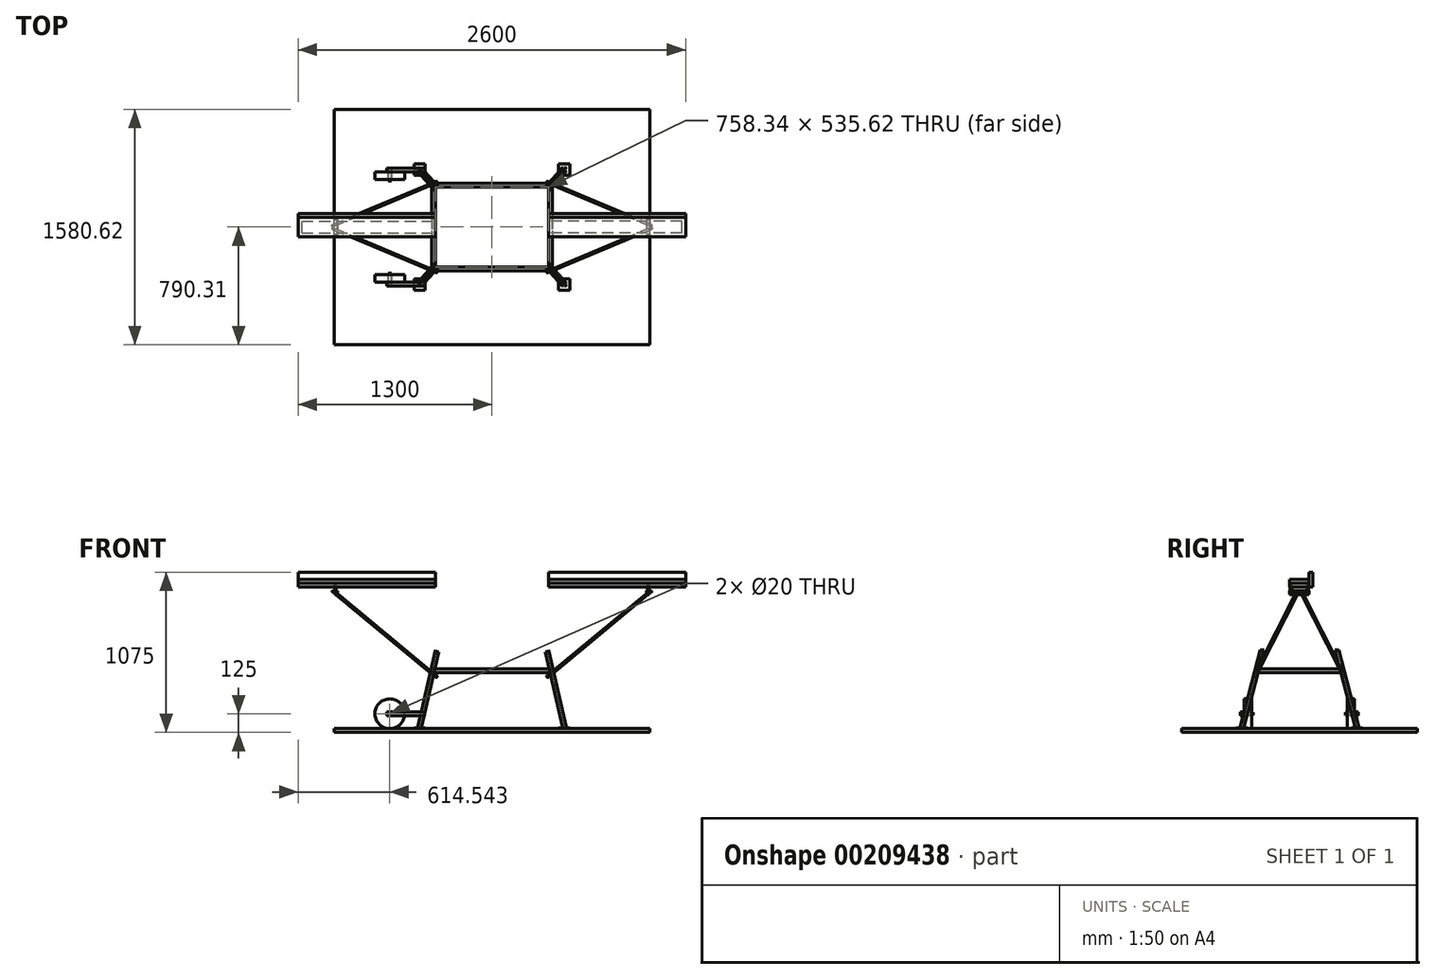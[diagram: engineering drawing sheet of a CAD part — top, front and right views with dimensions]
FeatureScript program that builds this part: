
annotation { "Feature Type Name" : "Feature", "Feature Type Description" : "" }
export const myFeature = defineFeature(function(context is Context, id is Id, definition is map)
    precondition{}
    {
        {
            var Q0;
            Q0=qCreatedBy(makeId("Top.planeOp"),FACE);
            var sketch = newSketch(context, id + "F0", { "sketchPlane" : qUnion([Q0])});
            skLineSegment(sketch, "E0.bottom", {"start": v(300, -175) * mm, "end": v(-300, -175) * mm});
            skLineSegment(sketch, "E0.top", {"start": v(300, 175) * mm, "end": v(-300, 175) * mm});
            skLineSegment(sketch, "E0.left", {"start": v(300, -175) * mm, "end": v(300, 175) * mm});
            skLineSegment(sketch, "E0.right", {"start": v(-300, -175) * mm, "end": v(-300, 175) * mm});
            skPoint(sketch, "E0.middle", {"position": v(0, 0) * mm});
            skSolve(sketch);
        }
        {
            var Q0;
            Q0 = qSketchRegion(id + "F0", true);
            extrude(context, id + "F1", {"entities" : qUnion([Q0]), "depth" : 100 * mm});
        }
        {
            var Q0;
            Q0=qCreatedBy(makeId("Top.planeOp"),FACE);
            cPlane(context, id + "F2", {"entities" : qUnion([Q0]), "cplaneType" : CPlaneType.OFFSET, "offset" : 900 * mm, "oppositeDirection" : true, "width" : 150 * mm, "height" : 150 * mm});
        }
        {
            var Q0;
            Q0=qCreatedBy(id+"F2.planeOp",FACE);
            var sketch = newSketch(context, id + "F3", { "sketchPlane" : qUnion([Q0])});
            skLineSegment(sketch, "E1.bottom", {"start": v(1059.42, -790.3) * mm, "end": v(-1059.42, -790.3) * mm});
            skLineSegment(sketch, "E1.top", {"start": v(1059.42, 790.3) * mm, "end": v(-1059.42, 790.3) * mm});
            skLineSegment(sketch, "E1.left", {"start": v(1059.42, -790.3) * mm, "end": v(1059.42, 790.3) * mm});
            skLineSegment(sketch, "E1.right", {"start": v(-1059.42, -790.3) * mm, "end": v(-1059.42, 790.3) * mm});
            skPoint(sketch, "E1.middle", {"position": v(0, 0) * mm});
            skSolve(sketch);
        }
        {
            var Q0;
            Q0 = qSketchRegion(id + "F3", true);
            extrude(context, id + "F4", {"entities" : qUnion([Q0]), "oppositeDirection" : true, "depth" : 25 * mm});
        }
        {
            var Q0;
            Q0=makeQuery(id+"F1.opExtrude","CAP_FACE",FACE,{"disambiguationData":[OSD([sQuery(id+"F0.wireOp",EDGE,"E0.bottom"),sQuery(id+"F0.wireOp",EDGE,"E0.top"),sQuery(id+"F0.wireOp",EDGE,"E0.left"),sQuery(id+"F0.wireOp",EDGE,"E0.right")])],"isStart":true});
            var sketch = newSketch(context, id + "F5", { "sketchPlane" : qUnion([Q0])});
            skLineSegment(sketch, "E2.bottom", {"start": v(-300, 175) * mm, "end": v(300, 175) * mm});
            skLineSegment(sketch, "E2.top", {"start": v(-300, -175) * mm, "end": v(300, -175) * mm});
            skLineSegment(sketch, "E2.left", {"start": v(-300, 175) * mm, "end": v(-300, -175) * mm});
            skLineSegment(sketch, "E2.right", {"start": v(300, 175) * mm, "end": v(300, -175) * mm});
            skLineSegment(sketch, "E3.0", {"start": v(-275, 150) * mm, "end": v(275, 150) * mm});
            skLineSegment(sketch, "E3.1", {"start": v(-275, 150) * mm, "end": v(-275, -150) * mm});
            skLineSegment(sketch, "E3.2", {"start": v(-275, -150) * mm, "end": v(275, -150) * mm});
            skLineSegment(sketch, "E3.3", {"start": v(275, 150) * mm, "end": v(275, -150) * mm});
            skSolve(sketch);
        }
        {
            var Q0;
            Q0 = qSketchRegion(id + "F5", true);
            extrude(context, id + "F6", {"entities" : qUnion([Q0]), "depth" : 25 * mm});
        }
        {
            var Q0;
            Q0=makeQuery(id+"F6.opExtrude","CAP_FACE",FACE,{"disambiguationData":[OSD([sQuery(id+"F5.wireOp",EDGE,"E2.bottom"),sQuery(id+"F5.wireOp",EDGE,"E2.top"),sQuery(id+"F5.wireOp",EDGE,"E2.left"),sQuery(id+"F5.wireOp",EDGE,"E2.right"),sQuery(id+"F5.wireOp",EDGE,"E3.0"),sQuery(id+"F5.wireOp",EDGE,"E3.1"),sQuery(id+"F5.wireOp",EDGE,"E3.2"),sQuery(id+"F5.wireOp",EDGE,"E3.3")])],"isStart":false});
            var sketch = newSketch(context, id + "F7", { "sketchPlane" : qUnion([Q0])});
            skLineSegment(sketch, "E4.bottom", {"start": v(-297, 172) * mm, "end": v(297, 172) * mm});
            skLineSegment(sketch, "E4.top", {"start": v(-297, -172) * mm, "end": v(297, -172) * mm});
            skLineSegment(sketch, "E4.left", {"start": v(-297, 172) * mm, "end": v(-297, -172) * mm});
            skLineSegment(sketch, "E4.right", {"start": v(297, 172) * mm, "end": v(297, -172) * mm});
            skSolve(sketch);
        }
        {
            var Q0;
            Q0 = qSketchRegion(id + "F7", true);
            extrude(context, id + "F8", {"entities" : qUnion([Q0]), "operationType" : NewBodyOperationType.REMOVE, "oppositeDirection" : true, "depth" : 22 * mm});
        }
        {
            var Q0;
            Q0=makeQuery(id+"F4.opExtrude","CAP_FACE",FACE,{"disambiguationData":[OSD([sQuery(id+"F3.wireOp",EDGE,"E1.bottom"),sQuery(id+"F3.wireOp",EDGE,"E1.top"),sQuery(id+"F3.wireOp",EDGE,"E1.left"),sQuery(id+"F3.wireOp",EDGE,"E1.right")])],"isStart":true});
            var sketch = newSketch(context, id + "F9", { "sketchPlane" : qUnion([Q0])});
            skLineSegment(sketch, "E5.bottom", {"start": v(500, -400) * mm, "end": v(-500, -400) * mm, "construction": true});
            skLineSegment(sketch, "E5.top", {"start": v(500, 400) * mm, "end": v(-500, 400) * mm, "construction": true});
            skLineSegment(sketch, "E5.left", {"start": v(500, -400) * mm, "end": v(500, 400) * mm, "construction": true});
            skLineSegment(sketch, "E5.right", {"start": v(-500, -400) * mm, "end": v(-500, 400) * mm, "construction": true});
            skPoint(sketch, "E5.middle", {"position": v(0, 0) * mm});
            skLineSegment(sketch, "E6", {"start": v(-500, -375) * mm, "end": v(-500, -400) * mm});
            skLineSegment(sketch, "E7", {"start": v(-500, -400) * mm, "end": v(-475, -400) * mm});
            skLineSegment(sketch, "E8", {"start": v(-475, -400) * mm, "end": v(-475, -397) * mm});
            skLineSegment(sketch, "E9", {"start": v(-475, -397) * mm, "end": v(-497, -397) * mm});
            skLineSegment(sketch, "E10", {"start": v(-497, -397) * mm, "end": v(-497, -375) * mm});
            skLineSegment(sketch, "E11", {"start": v(-497, -375) * mm, "end": v(-500, -375) * mm});
            skLineSegment(sketch, "E12", {"start": v(-868.34, 0) * mm, "end": v(770.25, 0) * mm, "construction": true});
            skLineSegment(sketch, "E13", {"start": v(0, 516.11) * mm, "end": v(0, -693.23) * mm, "construction": true});
            skPoint(sketch, "E13.startSnap0", {"position": v(0, 400) * mm});
            skSolve(sketch);
        }
        {
            var Q0;
            Q0=makeQuery(id+"F6.opExtrude","CAP_FACE",FACE,{"disambiguationData":[OSD([sQuery(id+"F5.wireOp",EDGE,"E2.bottom"),sQuery(id+"F5.wireOp",EDGE,"E2.top"),sQuery(id+"F5.wireOp",EDGE,"E2.left"),sQuery(id+"F5.wireOp",EDGE,"E2.right"),sQuery(id+"F5.wireOp",EDGE,"E3.0"),sQuery(id+"F5.wireOp",EDGE,"E3.1"),sQuery(id+"F5.wireOp",EDGE,"E3.2"),sQuery(id+"F5.wireOp",EDGE,"E3.3")])],"isStart":false});
            var sketch = newSketch(context, id + "F10", { "sketchPlane" : qUnion([Q0])});
            skLineSegment(sketch, "E14", {"start": v(-300, 175) * mm, "end": v(-300, 150) * mm});
            skLineSegment(sketch, "E15", {"start": v(-300, 150) * mm, "end": v(-297, 150) * mm});
            skLineSegment(sketch, "E16", {"start": v(-297, 150) * mm, "end": v(-297, 172) * mm});
            skLineSegment(sketch, "E17", {"start": v(-297, 172) * mm, "end": v(-275, 172) * mm});
            skLineSegment(sketch, "E18", {"start": v(-275, 172) * mm, "end": v(-275, 175) * mm});
            skLineSegment(sketch, "E19", {"start": v(-275, 175) * mm, "end": v(-300, 175) * mm});
            skSolve(sketch);
        }
        {
            var Q1;
            Q1 = qSketchRegion(id + "F9", true);
            var Q2;
            Q2 = qSketchRegion(id + "F10", true);
            loft(context, id + "F11", {"sheetProfilesArray" : [{ "sheetProfileEntities" : qUnion([Q1]) }, { "sheetProfileEntities" : qUnion([Q2]) }]});
        }
        {
            var Q0;
            Q0=makeQuery(id+"F11.opLoft","SWEPT_BODY",BODY,{"disambiguationData":[OSD([makeQuery(id+"F9.imprint","IMPRINT",FACE,{"disambiguationData":[TD([[makeQuery(id+"F9.imprint","IMPRINT",EDGE,{"derivedFrom":sQuery(id+"F9.wireOp",EDGE,"E6")}),1.0]])]}),makeQuery(id+"F10.imprint","IMPRINT",FACE,{"disambiguationData":[TD([[makeQuery(id+"F10.imprint","IMPRINT",EDGE,{"derivedFrom":sQuery(id+"F10.wireOp",EDGE,"E14")}),1.0]])]})])]});
            var Q1;
            Q1=qCreatedBy(makeId("Right.planeOp"),FACE);
            mirror(context, id + "F12", {"entities" : qUnion([Q0]), "mirrorPlane" : qUnion([Q1])});
        }
        {
            var Q0;
            Q0=makeQuery(id+"F11.opLoft","SWEPT_BODY",BODY,{"disambiguationData":[OSD([makeQuery(id+"F9.imprint","IMPRINT",FACE,{"disambiguationData":[TD([[makeQuery(id+"F9.imprint","IMPRINT",EDGE,{"derivedFrom":sQuery(id+"F9.wireOp",EDGE,"E6")}),1.0]])]}),makeQuery(id+"F10.imprint","IMPRINT",FACE,{"disambiguationData":[TD([[makeQuery(id+"F10.imprint","IMPRINT",EDGE,{"derivedFrom":sQuery(id+"F10.wireOp",EDGE,"E14")}),1.0]])]})])]});
            var Q1;
            Q1=makeQuery(id+"F12.opPattern","COPY",BODY,{"derivedFrom":makeQuery(id+"F11.opLoft","SWEPT_BODY",BODY,{"disambiguationData":[OSD([makeQuery(id+"F9.imprint","IMPRINT",FACE,{"disambiguationData":[TD([[makeQuery(id+"F9.imprint","IMPRINT",EDGE,{"derivedFrom":sQuery(id+"F9.wireOp",EDGE,"E6")}),1.0]])]}),makeQuery(id+"F10.imprint","IMPRINT",FACE,{"disambiguationData":[TD([[makeQuery(id+"F10.imprint","IMPRINT",EDGE,{"derivedFrom":sQuery(id+"F10.wireOp",EDGE,"E14")}),1.0]])]})])]}),"instanceName":"1"});
            var Q2;
            Q2=qCreatedBy(makeId("Front.planeOp"),FACE);
            mirror(context, id + "F13", {"entities" : qUnion([Q0, Q1]), "mirrorPlane" : qUnion([Q2])});
        }
        {
            assignVariable(context, id + "F14", {"name" : "MidLevel", "anyValue" : 500});
        }
        {
            var Q0;
            Q0=qCreatedBy(makeId("Top.planeOp"),FACE);
            cPlane(context, id + "F15", {"entities" : qUnion([Q0]), "cplaneType" : CPlaneType.OFFSET, "offset" : (getVariable(context, 'MidLevel')) * mm, "oppositeDirection" : true, "width" : 150 * mm, "height" : 150 * mm});
        }
        {
            var Q0;
            Q0=qCreatedBy(id+"F15.planeOp",FACE);
            var sketch = newSketch(context, id + "F16", { "sketchPlane" : qUnion([Q0])});
            skLineSegment(sketch, "E20.bottom", {"start": v(404.17, 292.8) * mm, "end": v(-404.17, 292.8) * mm});
            skLineSegment(sketch, "E20.top", {"start": v(404.17, -292.8) * mm, "end": v(-404.17, -292.8) * mm});
            skLineSegment(sketch, "E20.left", {"start": v(404.17, 292.8) * mm, "end": v(404.17, -292.8) * mm});
            skLineSegment(sketch, "E20.right", {"start": v(-404.17, 292.8) * mm, "end": v(-404.17, -292.8) * mm});
            skPoint(sketch, "E20.middle", {"position": v(0, 0) * mm});
            skSolve(sketch);
        }
        {
            var Q0;
            Q0 = qSketchRegion(id + "F16", true);
            extrude(context, id + "F17", {"entities" : qUnion([Q0]), "oppositeDirection" : true, "depth" : 25 * mm});
        }
        {
            var Q0;
            Q0=qCreatedBy(id+"F2.planeOp",FACE);
            var sketch = newSketch(context, id + "F18", { "sketchPlane" : qUnion([Q0])});
            skLineSegment(sketch, "E21.bottom", {"start": v(-522.96, -423.3) * mm, "end": v(-447.96, -423.3) * mm});
            skLineSegment(sketch, "E21.top", {"start": v(-522.96, -348.3) * mm, "end": v(-447.96, -348.3) * mm});
            skLineSegment(sketch, "E21.left", {"start": v(-522.96, -423.3) * mm, "end": v(-522.96, -348.3) * mm});
            skLineSegment(sketch, "E21.right", {"start": v(-447.96, -423.3) * mm, "end": v(-447.96, -348.3) * mm});
            skSolve(sketch);
        }
        {
            var Q0;
            Q0 = qSketchRegion(id + "F18", true);
            extrude(context, id + "F19", {"entities" : qUnion([Q0]), "depth" : 3 * mm});
        }
        {
            var Q0;
            Q0=makeQuery(id+"F19.opExtrude","SWEPT_BODY",BODY,{"disambiguationData":[OSD([sQuery(id+"F18.wireOp",EDGE,"E21.bottom"),sQuery(id+"F18.wireOp",EDGE,"E21.top"),sQuery(id+"F18.wireOp",EDGE,"E21.left"),sQuery(id+"F18.wireOp",EDGE,"E21.right")])]});
            var Q1;
            Q1=qCreatedBy(makeId("Front.planeOp"),FACE);
            mirror(context, id + "F20", {"entities" : qUnion([Q0]), "mirrorPlane" : qUnion([Q1])});
        }
        {
            var Q0;
            Q0=makeQuery(id+"F20.opPattern","COPY",BODY,{"derivedFrom":makeQuery(id+"F19.opExtrude","SWEPT_BODY",BODY,{"disambiguationData":[OSD([sQuery(id+"F18.wireOp",EDGE,"E21.bottom"),sQuery(id+"F18.wireOp",EDGE,"E21.top"),sQuery(id+"F18.wireOp",EDGE,"E21.left"),sQuery(id+"F18.wireOp",EDGE,"E21.right")])]}),"instanceName":"1"});
            var Q1;
            Q1=makeQuery(id+"F19.opExtrude","SWEPT_BODY",BODY,{"disambiguationData":[OSD([sQuery(id+"F18.wireOp",EDGE,"E21.bottom"),sQuery(id+"F18.wireOp",EDGE,"E21.top"),sQuery(id+"F18.wireOp",EDGE,"E21.left"),sQuery(id+"F18.wireOp",EDGE,"E21.right")])]});
            var Q2;
            Q2=qCreatedBy(makeId("Right.planeOp"),FACE);
            mirror(context, id + "F21", {"entities" : qUnion([Q0, Q1]), "mirrorPlane" : qUnion([Q2])});
        }
        {
            var Q0;
            Q0=makeQuery(id+"F1.opExtrude","CAP_FACE",FACE,{"disambiguationData":[OSD([sQuery(id+"F0.wireOp",EDGE,"E0.bottom"),sQuery(id+"F0.wireOp",EDGE,"E0.top"),sQuery(id+"F0.wireOp",EDGE,"E0.left"),sQuery(id+"F0.wireOp",EDGE,"E0.right")])],"isStart":false});
            var sketch = newSketch(context, id + "F22", { "sketchPlane" : qUnion([Q0])});
            skLineSegment(sketch, "E22.bottom", {"start": v(-1300, 65) * mm, "end": v(-300, 65) * mm});
            skLineSegment(sketch, "E22.top", {"start": v(-1300, -65) * mm, "end": v(-300, -65) * mm});
            skLineSegment(sketch, "E22.left", {"start": v(-1300, 65) * mm, "end": v(-1300, -65) * mm});
            skLineSegment(sketch, "E22.right", {"start": v(-300, 65) * mm, "end": v(-300, -65) * mm});
            skLineSegment(sketch, "E23", {"start": v(0, 0) * mm, "end": v(-555.69, 0) * mm, "construction": true});
            skSolve(sketch);
        }
        {
            var Q0;
            Q0 = qSketchRegion(id + "F22", true);
            extrude(context, id + "F23", {"entities" : qUnion([Q0]), "oppositeDirection" : true, "depth" : 25 * mm});
        }
        {
            var Q0;
            Q0=makeQuery(id+"F23.opExtrude","CAP_FACE",FACE,{"disambiguationData":[OSD([sQuery(id+"F22.wireOp",EDGE,"E22.bottom"),sQuery(id+"F22.wireOp",EDGE,"E22.top"),sQuery(id+"F22.wireOp",EDGE,"E22.left"),sQuery(id+"F22.wireOp",EDGE,"E22.right")])],"isStart":false});
            var sketch = newSketch(context, id + "F24", { "sketchPlane" : qUnion([Q0])});
            skLineSegment(sketch, "E24.bottom", {"start": v(-1300, 65) * mm, "end": v(-300, 65) * mm});
            skLineSegment(sketch, "E24.top", {"start": v(-1300, -65) * mm, "end": v(-300, -65) * mm});
            skLineSegment(sketch, "E24.left", {"start": v(-1300, 65) * mm, "end": v(-1300, -65) * mm});
            skLineSegment(sketch, "E24.right", {"start": v(-300, 65) * mm, "end": v(-300, -65) * mm});
            skLineSegment(sketch, "E25.0", {"start": v(-1275, 40) * mm, "end": v(-325, 40) * mm});
            skLineSegment(sketch, "E25.1", {"start": v(-1275, 40) * mm, "end": v(-1275, -40) * mm});
            skLineSegment(sketch, "E25.2", {"start": v(-1275, -40) * mm, "end": v(-325, -40) * mm});
            skLineSegment(sketch, "E25.3", {"start": v(-325, 40) * mm, "end": v(-325, -40) * mm});
            skSolve(sketch);
        }
        {
            var Q0;
            Q0 = qSketchRegion(id + "F24", true);
            extrude(context, id + "F25", {"entities" : qUnion([Q0]), "depth" : 25 * mm});
        }
        {
            var Q0;
            Q0=makeQuery(id+"F25.opExtrude","CAP_FACE",FACE,{"disambiguationData":[OSD([sQuery(id+"F24.wireOp",EDGE,"E24.bottom"),sQuery(id+"F24.wireOp",EDGE,"E24.top"),sQuery(id+"F24.wireOp",EDGE,"E24.left"),sQuery(id+"F24.wireOp",EDGE,"E24.right"),sQuery(id+"F24.wireOp",EDGE,"E25.0"),sQuery(id+"F24.wireOp",EDGE,"E25.1"),sQuery(id+"F24.wireOp",EDGE,"E25.2"),sQuery(id+"F24.wireOp",EDGE,"E25.3")])],"isStart":false});
            var sketch = newSketch(context, id + "F26", { "sketchPlane" : qUnion([Q0])});
            skLineSegment(sketch, "E26.bottom", {"start": v(-1297, 62) * mm, "end": v(-303, 62) * mm});
            skLineSegment(sketch, "E26.top", {"start": v(-1297, -62) * mm, "end": v(-303, -62) * mm});
            skLineSegment(sketch, "E26.left", {"start": v(-1297, 62) * mm, "end": v(-1297, -62) * mm});
            skLineSegment(sketch, "E26.right", {"start": v(-303, 62) * mm, "end": v(-303, -62) * mm});
            skSolve(sketch);
        }
        {
            var Q0;
            Q0 = qSketchRegion(id + "F26", true);
            extrude(context, id + "F27", {"entities" : qUnion([Q0]), "operationType" : NewBodyOperationType.REMOVE, "oppositeDirection" : true, "depth" : 22 * mm});
        }
        {
            var Q0;
            Q0=makeQuery(id+"F25.opExtrude","SWEPT_FACE",FACE,{"disambiguationData":[OSD([sQuery(id+"F24.wireOp",EDGE,"E24.top")])]});
            var sketch = newSketch(context, id + "F28", { "sketchPlane" : qUnion([Q0])});
            skLineSegment(sketch, "E27.bottom", {"start": v(300, 50) * mm, "end": v(1300, 50) * mm});
            skLineSegment(sketch, "E27.top", {"start": v(300, 150) * mm, "end": v(1300, 150) * mm});
            skLineSegment(sketch, "E27.left", {"start": v(300, 50) * mm, "end": v(300, 150) * mm});
            skLineSegment(sketch, "E27.right", {"start": v(1300, 50) * mm, "end": v(1300, 150) * mm});
            skSolve(sketch);
        }
        {
            var Q0;
            Q0 = qSketchRegion(id + "F28", true);
            extrude(context, id + "F29", {"entities" : qUnion([Q0]), "depth" : 25 * mm});
        }
        {
            var Q0;
            Q0=makeQuery(id+"F25.opExtrude","CAP_FACE",FACE,{"disambiguationData":[OSD([sQuery(id+"F24.wireOp",EDGE,"E24.bottom"),sQuery(id+"F24.wireOp",EDGE,"E24.top"),sQuery(id+"F24.wireOp",EDGE,"E24.left"),sQuery(id+"F24.wireOp",EDGE,"E24.right"),sQuery(id+"F24.wireOp",EDGE,"E25.0"),sQuery(id+"F24.wireOp",EDGE,"E25.1"),sQuery(id+"F24.wireOp",EDGE,"E25.2"),sQuery(id+"F24.wireOp",EDGE,"E25.3")])],"isStart":false});
            var sketch = newSketch(context, id + "F30", { "sketchPlane" : qUnion([Q0])});
            skCircle(sketch, "E28", {"center": v(-1050, 56) * mm, "radius": 6 * mm});
            skSolve(sketch);
        }
        {
            var Q0;
            Q0 = qSketchRegion(id + "F30", true);
            var Q1;
            Q1=makeQuery(id+"F23.opExtrude","CAP_FACE",FACE,{"disambiguationData":[OSD([sQuery(id+"F22.wireOp",EDGE,"E22.bottom"),sQuery(id+"F22.wireOp",EDGE,"E22.top"),sQuery(id+"F22.wireOp",EDGE,"E22.left"),sQuery(id+"F22.wireOp",EDGE,"E22.right")])],"isStart":false});
            extrude(context, id + "F31", {"entities" : qUnion([Q0]), "depth" : 50 * mm, "hasSecondDirection" : true, "secondDirectionBound" : SecondDirectionBoundingType.UP_TO_SURFACE, "secondDirectionOppositeDirection" : true, "secondDirectionBoundEntityFace" : qUnion([Q1]), "secondDirectionDepth" : 25 * mm});
        }
        {
            var Q0;
            Q0=makeQuery(id+"F31.opExtrude","SWEPT_BODY",BODY,{"disambiguationData":[OSD([sQuery(id+"F30.wireOp",EDGE,"E28")])]});
            var Q1;
            Q1=qCreatedBy(makeId("Front.planeOp"),FACE);
            mirror(context, id + "F32", {"entities" : qUnion([Q0]), "mirrorPlane" : qUnion([Q1])});
        }
        {
            var Q0;
            Q0=makeQuery(id+"F25.opExtrude","SWEPT_FACE",FACE,{"disambiguationData":[OSD([sQuery(id+"F24.wireOp",EDGE,"E24.bottom")])]});
            var sketch = newSketch(context, id + "F33", { "sketchPlane" : qUnion([Q0])});
            skLineSegment(sketch, "E29", {"start": v(-1060.82, 25) * mm, "end": v(-1035.82, 25) * mm});
            skLineSegment(sketch, "E30", {"start": v(-1035.82, 25) * mm, "end": v(-1035.82, 0) * mm});
            skLineSegment(sketch, "E31", {"start": v(-1035.82, 0) * mm, "end": v(-1038.82, 0) * mm});
            skLineSegment(sketch, "E32", {"start": v(-1038.82, 0) * mm, "end": v(-1038.82, 22) * mm});
            skLineSegment(sketch, "E33", {"start": v(-1038.82, 22) * mm, "end": v(-1060.82, 22) * mm});
            skLineSegment(sketch, "E34", {"start": v(-1060.82, 22) * mm, "end": v(-1060.82, 25) * mm});
            skSolve(sketch);
        }
        {
            var Q0;
            Q0 = qSketchRegion(id + "F33", true);
            var Q1;
            Q1=makeQuery(id+"F25.opExtrude","SWEPT_FACE",FACE,{"disambiguationData":[OSD([sQuery(id+"F24.wireOp",EDGE,"E24.top")])]});
            extrude(context, id + "F34", {"entities" : qUnion([Q0]), "endBound" : BoundingType.UP_TO_SURFACE, "oppositeDirection" : true, "endBoundEntityFace" : qUnion([Q1]), "depth" : 25 * mm});
        }
        {
            var Q0;
            Q0=makeQuery(id+"F34.opExtrude","SWEPT_EDGE",EDGE,{"disambiguationData":[OSD([sQuery(id+"F33.wireOp",EDGE,"E31"),sQuery(id+"F33.wireOp",EDGE,"E32")])]});
            cPoint(context, id + "F35", {"entities" : qUnion([Q0]), "parameter" : 0.5});
        }
        {
            var Q0;
            Q0=makeQuery(id+"F17.opExtrude","CAP_VERTEX",VERTEX,{"disambiguationData":[OSD([sQuery(id+"F16.wireOp",EDGE,"E20.bottom"),sQuery(id+"F16.wireOp",EDGE,"E20.right")])],"isStart":false});
            var Q1;
            Q1=makeQuery(id+"F17.opExtrude","CAP_VERTEX",VERTEX,{"disambiguationData":[OSD([sQuery(id+"F16.wireOp",EDGE,"E20.top"),sQuery(id+"F16.wireOp",EDGE,"E20.right")])],"isStart":false});
            var Q2;
            Q2 = qCreatedBy(id + "F35" ,VERTEX);
            cPlane(context, id + "F36", {"entities" : qUnion([Q0, Q1, Q2]), "cplaneType" : CPlaneType.THREE_POINT, "offset" : 25 * mm, "width" : 150 * mm, "height" : 150 * mm});
        }
        {
            var Q0;
            Q0=qCreatedBy(id+"F36.planeOp",FACE);
            var sketch = newSketch(context, id + "F37", { "sketchPlane" : qUnion([Q0])});
            skLineSegment(sketch, "E35", {"start": v(18.66, -286.5) * mm, "end": v(-806.2, -20.03) * mm});
            skSolve(sketch);
        }
        {
            var Q0;
            Q0=sQuery(id+"F37.wireOp",EDGE,"E35");
            var Q1;
            Q1=sQuery(id+"F37.wireOp",VERTEX,"E35.start");
            cPlane(context, id + "F38", {"entities" : qUnion([Q0, Q1]), "cplaneType" : CPlaneType.LINE_POINT, "offset" : 25 * mm, "width" : 150 * mm, "height" : 150 * mm});
        }
        {
            var Q0;
            Q0=qCreatedBy(id+"F38.planeOp",FACE);
            var sketch = newSketch(context, id + "F39", { "sketchPlane" : qUnion([Q0])});
            skCircle(sketch, "E36", {"center": v(266.9, -662.15) * mm, "radius": 6 * mm});
            skCircle(sketch, "E37", {"center": v(266.9, -662.15) * mm, "radius": 8 * mm});
            skSolve(sketch);
        }
        {
            var Q0;
            Q0 = qSketchRegion(id + "F39", true);
            extrude(context, id + "F40", {"entities" : qUnion([Q0]), "depth" : 15 * mm, "hasSecondDirection" : true, "secondDirectionOppositeDirection" : true, "secondDirectionDepth" : 35 * mm});
        }
        {
            var Q0;
            Q0=qCreatedBy(id+"F38.planeOp",FACE);
            var sketch = newSketch(context, id + "F41", { "sketchPlane" : qUnion([Q0])});
            skCircle(sketch, "E38", {"center": v(266.9, -662.15) * mm, "radius": 6 * mm});
            skSolve(sketch);
        }
        {
            var Q0;
            Q0 = qSketchRegion(id + "F41", true);
            var Q1;
            Q1=makeQuery(id+"F34.opExtrude","SWEPT_FACE",FACE,{"disambiguationData":[OSD([sQuery(id+"F33.wireOp",EDGE,"E33")])]});
            extrude(context, id + "F42", {"entities" : qUnion([Q0]), "endBound" : BoundingType.UP_TO_SURFACE, "endBoundEntityFace" : qUnion([Q1]), "depth" : 25 * mm, "hasSecondDirection" : true, "secondDirectionOppositeDirection" : true, "secondDirectionDepth" : 50 * mm});
        }
        {
            var Q0;
            Q0=makeQuery(id+"F42.opExtrude","SWEPT_BODY",BODY,{"disambiguationData":[OSD([sQuery(id+"F41.wireOp",EDGE,"E38")])]});
            var Q1;
            Q1=makeQuery(id+"F40.opExtrude","SWEPT_BODY",BODY,{"disambiguationData":[OSD([sQuery(id+"F39.wireOp",EDGE,"E36"),sQuery(id+"F39.wireOp",EDGE,"E37")])]});
            var Q2;
            Q2=qCreatedBy(makeId("Front.planeOp"),FACE);
            mirror(context, id + "F43", {"entities" : qUnion([Q0, Q1]), "mirrorPlane" : qUnion([Q2])});
        }
        {
            var Q0;
            Q0=makeQuery(id+"F34.opExtrude","SWEPT_BODY",BODY,{"disambiguationData":[OSD([sQuery(id+"F33.wireOp",EDGE,"E29"),sQuery(id+"F33.wireOp",EDGE,"E30"),sQuery(id+"F33.wireOp",EDGE,"E31"),sQuery(id+"F33.wireOp",EDGE,"E32"),sQuery(id+"F33.wireOp",EDGE,"E33"),sQuery(id+"F33.wireOp",EDGE,"E34")])]});
            var Q1;
            Q1=makeQuery(id+"F25.opExtrude","CAP_EDGE",EDGE,{"disambiguationData":[OSD([sQuery(id+"F24.wireOp",EDGE,"E24.bottom")])],"isStart":false});
            transform(context, id + "F44", {"entities" : qUnion([Q0]), "transformType" : TransformType.TRANSLATION_DISTANCE, "transformDirection" : qUnion([Q1]), "distance" : 735 * mm, "makeCopy" : true});
        }
        {
            var Q0;
            Q0=makeQuery(id+"F44.opPattern","COPY",BODY,{"derivedFrom":makeQuery(id+"F34.opExtrude","SWEPT_BODY",BODY,{"disambiguationData":[OSD([sQuery(id+"F33.wireOp",EDGE,"E29"),sQuery(id+"F33.wireOp",EDGE,"E30"),sQuery(id+"F33.wireOp",EDGE,"E31"),sQuery(id+"F33.wireOp",EDGE,"E32"),sQuery(id+"F33.wireOp",EDGE,"E33"),sQuery(id+"F33.wireOp",EDGE,"E34")])]}),"instanceName":"1"});
            var Q1;
            Q1=makeQuery(id+"F6.opExtrude","SWEPT_EDGE",EDGE,{"disambiguationData":[OSD([sQuery(id+"F5.wireOp",EDGE,"E2.bottom"),sQuery(id+"F5.wireOp",EDGE,"E2.left")])]});
            transform(context, id + "F45", {"entities" : qUnion([Q0]), "transformType" : TransformType.TRANSLATION_DISTANCE, "transformDirection" : qUnion([Q1]), "distance" : 25 * mm, "oppositeDirection" : true, "makeCopy" : false});
        }
        {
            var Q0;
            Q0=makeQuery(id+"F25.opExtrude","CAP_FACE",FACE,{"disambiguationData":[OSD([sQuery(id+"F24.wireOp",EDGE,"E24.bottom"),sQuery(id+"F24.wireOp",EDGE,"E24.top"),sQuery(id+"F24.wireOp",EDGE,"E24.left"),sQuery(id+"F24.wireOp",EDGE,"E24.right"),sQuery(id+"F24.wireOp",EDGE,"E25.0"),sQuery(id+"F24.wireOp",EDGE,"E25.1"),sQuery(id+"F24.wireOp",EDGE,"E25.2"),sQuery(id+"F24.wireOp",EDGE,"E25.3")])],"isStart":false});
            var sketch = newSketch(context, id + "F46", { "sketchPlane" : qUnion([Q0])});
            skCircle(sketch, "E39", {"center": v(-318, -56) * mm, "radius": 6 * mm});
            skCircle(sketch, "E40", {"center": v(-318, 56) * mm, "radius": 6 * mm});
            skSolve(sketch);
        }
        {
            var Q0;
            Q0 = qSketchRegion(id + "F46", true);
            var Q1;
            Q1=makeQuery(id+"F23.opExtrude","CAP_FACE",FACE,{"disambiguationData":[OSD([sQuery(id+"F22.wireOp",EDGE,"E22.bottom"),sQuery(id+"F22.wireOp",EDGE,"E22.top"),sQuery(id+"F22.wireOp",EDGE,"E22.left"),sQuery(id+"F22.wireOp",EDGE,"E22.right")])],"isStart":false});
            extrude(context, id + "F47", {"entities" : qUnion([Q0]), "depth" : 75 * mm, "hasSecondDirection" : true, "secondDirectionBound" : SecondDirectionBoundingType.UP_TO_SURFACE, "secondDirectionOppositeDirection" : true, "secondDirectionBoundEntityFace" : qUnion([Q1]), "secondDirectionDepth" : 25 * mm});
        }
        {
            var Q0;
            Q0=makeQuery(id+"F44.opPattern","COPY",FACE,{"derivedFrom":makeQuery(id+"F34.opExtrude","SWEPT_FACE",FACE,{"disambiguationData":[OSD([sQuery(id+"F33.wireOp",EDGE,"E32")])]}),"instanceName":"1"});
            var sketch = newSketch(context, id + "F48", { "sketchPlane" : qUnion([Q0])});
            skArc(sketch, "E41", {"start": v(-47, -9) * mm, "mid": v(-52, -14) * mm, "end": v(-47, -19) * mm});
            skArc(sketch, "E42", {"start": v(-37, -19) * mm, "mid": v(-32, -14) * mm, "end": v(-37, -9) * mm});
            skLineSegment(sketch, "E43", {"start": v(-65, -14) * mm, "end": v(65, -14) * mm, "construction": true});
            skLineSegment(sketch, "E44", {"start": v(-47, -9) * mm, "end": v(-37, -9) * mm});
            skLineSegment(sketch, "E45", {"start": v(-47, -19) * mm, "end": v(-37, -19) * mm});
            skLineSegment(sketch, "E46", {"start": v(0, 11.66) * mm, "end": v(0, -35.96) * mm, "construction": true});
            skLineSegment(sketch, "E47.MirrorCS", {"start": v(47, -9) * mm, "end": v(37, -9) * mm});
            skArc(sketch, "E48.MirrorCS", {"start": v(37, -19) * mm, "mid": v(32, -14) * mm, "end": v(37, -9) * mm});
            skLineSegment(sketch, "E49.MirrorCS", {"start": v(47, -19) * mm, "end": v(37, -19) * mm});
            skArc(sketch, "E50.MirrorCS", {"start": v(47, -9) * mm, "mid": v(52, -14) * mm, "end": v(47, -19) * mm});
            skSolve(sketch);
        }
        {
            var Q0;
            Q0 = qSketchRegion(id + "F48", true);
            var Q1;
            Q1=makeQuery(id+"F6.opExtrude","SWEPT_FACE",FACE,{"disambiguationData":[OSD([sQuery(id+"F5.wireOp",EDGE,"E2.left")])]});
            extrude(context, id + "F49", {"entities" : qUnion([Q0]), "operationType" : NewBodyOperationType.REMOVE, "endBound" : BoundingType.UP_TO_SURFACE, "oppositeDirection" : true, "endBoundEntityFace" : qUnion([Q1]), "depth" : 25 * mm});
        }
        {
            var Q0;
            Q0=makeQuery(id+"F6.opExtrude","SWEPT_FACE",FACE,{"disambiguationData":[OSD([sQuery(id+"F5.wireOp",EDGE,"E2.left")])]});
            var sketch = newSketch(context, id + "F50", { "sketchPlane" : qUnion([Q0])});
            skCircle(sketch, "E51", {"center": v(-42, -14) * mm, "radius": 5 * mm});
            skCircle(sketch, "E52", {"center": v(42, -14) * mm, "radius": 5 * mm});
            skLineSegment(sketch, "E53", {"start": v(-94.72, -14) * mm, "end": v(93.71, -14) * mm, "construction": true});
            skLineSegment(sketch, "E54", {"start": v(-32, -3.86) * mm, "end": v(-32, -30.47) * mm, "construction": true});
            skLineSegment(sketch, "E55", {"start": v(-52, -3.07) * mm, "end": v(-52, -35.3) * mm, "construction": true});
            skLineSegment(sketch, "E56", {"start": v(32, -3.51) * mm, "end": v(32, -29.8) * mm, "construction": true});
            skLineSegment(sketch, "E57", {"start": v(52, -2.96) * mm, "end": v(52, -32.14) * mm, "construction": true});
            skLineSegment(sketch, "E58", {"start": v(42, -10.23) * mm, "end": v(42, -17.16) * mm, "construction": true});
            skLineSegment(sketch, "E59", {"start": v(-42, -9.75) * mm, "end": v(-42, -17.9) * mm, "construction": true});
            skSolve(sketch);
        }
        {
            var Q0;
            Q0 = qSketchRegion(id + "F50", true);
            extrude(context, id + "F51", {"entities" : qUnion([Q0]), "operationType" : NewBodyOperationType.REMOVE, "endBound" : BoundingType.THROUGH_ALL, "oppositeDirection" : true, "depth" : 25 * mm});
        }
        {
            var Q0;
            Q0=makeQuery(id+"F44.opPattern","COPY",BODY,{"derivedFrom":makeQuery(id+"F34.opExtrude","SWEPT_BODY",BODY,{"disambiguationData":[OSD([sQuery(id+"F33.wireOp",EDGE,"E29"),sQuery(id+"F33.wireOp",EDGE,"E30"),sQuery(id+"F33.wireOp",EDGE,"E31"),sQuery(id+"F33.wireOp",EDGE,"E32"),sQuery(id+"F33.wireOp",EDGE,"E33"),sQuery(id+"F33.wireOp",EDGE,"E34")])]}),"instanceName":"1"});
            var Q1;
            Q1=makeQuery(id+"F47.opExtrude","SWEPT_BODY",BODY,{"disambiguationData":[OSD([sQuery(id+"F46.wireOp",EDGE,"E39")])]});
            var Q2;
            Q2=makeQuery(id+"F47.opExtrude","SWEPT_BODY",BODY,{"disambiguationData":[OSD([sQuery(id+"F46.wireOp",EDGE,"E40")])]});
            var Q3;
            Q3=makeQuery(id+"F25.opExtrude","SWEPT_BODY",BODY,{"disambiguationData":[OSD([sQuery(id+"F24.wireOp",EDGE,"E24.bottom"),sQuery(id+"F24.wireOp",EDGE,"E24.top"),sQuery(id+"F24.wireOp",EDGE,"E24.left"),sQuery(id+"F24.wireOp",EDGE,"E24.right"),sQuery(id+"F24.wireOp",EDGE,"E25.0"),sQuery(id+"F24.wireOp",EDGE,"E25.1"),sQuery(id+"F24.wireOp",EDGE,"E25.2"),sQuery(id+"F24.wireOp",EDGE,"E25.3")])]});
            var Q4;
            Q4=makeQuery(id+"F23.opExtrude","SWEPT_BODY",BODY,{"disambiguationData":[OSD([sQuery(id+"F22.wireOp",EDGE,"E22.bottom"),sQuery(id+"F22.wireOp",EDGE,"E22.top"),sQuery(id+"F22.wireOp",EDGE,"E22.left"),sQuery(id+"F22.wireOp",EDGE,"E22.right")])]});
            var Q5;
            Q5=makeQuery(id+"F31.opExtrude","SWEPT_BODY",BODY,{"disambiguationData":[OSD([sQuery(id+"F30.wireOp",EDGE,"E28")])]});
            var Q6;
            Q6=makeQuery(id+"F32.opPattern","COPY",BODY,{"derivedFrom":makeQuery(id+"F31.opExtrude","SWEPT_BODY",BODY,{"disambiguationData":[OSD([sQuery(id+"F30.wireOp",EDGE,"E28")])]}),"instanceName":"1"});
            var Q7;
            Q7=makeQuery(id+"F34.opExtrude","SWEPT_BODY",BODY,{"disambiguationData":[OSD([sQuery(id+"F33.wireOp",EDGE,"E29"),sQuery(id+"F33.wireOp",EDGE,"E30"),sQuery(id+"F33.wireOp",EDGE,"E31"),sQuery(id+"F33.wireOp",EDGE,"E32"),sQuery(id+"F33.wireOp",EDGE,"E33"),sQuery(id+"F33.wireOp",EDGE,"E34")])]});
            var Q8;
            Q8=makeQuery(id+"F42.opExtrude","SWEPT_BODY",BODY,{"disambiguationData":[OSD([sQuery(id+"F41.wireOp",EDGE,"E38")])]});
            var Q9;
            Q9=makeQuery(id+"F43.opPattern","COPY",BODY,{"derivedFrom":makeQuery(id+"F42.opExtrude","SWEPT_BODY",BODY,{"disambiguationData":[OSD([sQuery(id+"F41.wireOp",EDGE,"E38")])]}),"instanceName":"1"});
            var Q10;
            Q10=makeQuery(id+"F43.opPattern","COPY",BODY,{"derivedFrom":makeQuery(id+"F40.opExtrude","SWEPT_BODY",BODY,{"disambiguationData":[OSD([sQuery(id+"F39.wireOp",EDGE,"E36"),sQuery(id+"F39.wireOp",EDGE,"E37")])]}),"instanceName":"1"});
            var Q11;
            Q11=makeQuery(id+"F40.opExtrude","SWEPT_BODY",BODY,{"disambiguationData":[OSD([sQuery(id+"F39.wireOp",EDGE,"E36"),sQuery(id+"F39.wireOp",EDGE,"E37")])]});
            var Q12;
            Q12=makeQuery(id+"F29.opExtrude","SWEPT_BODY",BODY,{"disambiguationData":[OSD([sQuery(id+"F28.wireOp",EDGE,"E27.bottom"),sQuery(id+"F28.wireOp",EDGE,"E27.top"),sQuery(id+"F28.wireOp",EDGE,"E27.left"),sQuery(id+"F28.wireOp",EDGE,"E27.right")])]});
            var Q13;
            Q13=qCreatedBy(makeId("Right.planeOp"),FACE);
            mirror(context, id + "F52", {"entities" : qUnion([Q0, Q1, Q2, Q3, Q4, Q5, Q6, Q7, Q8, Q9, Q10, Q11, Q12]), "mirrorPlane" : qUnion([Q13])});
        }
        {
            var Q0;
            Q0=qCreatedBy(makeId("Front.planeOp"),FACE);
            cPlane(context, id + "F53", {"entities" : qUnion([Q0]), "cplaneType" : CPlaneType.OFFSET, "offset" : 370 * mm, "width" : 150 * mm, "height" : 150 * mm});
        }
        {
            var Q0;
            Q0=qCreatedBy(id+"F53.planeOp",FACE);
            var sketch = newSketch(context, id + "F54", { "sketchPlane" : qUnion([Q0])});
            skCircle(sketch, "E60", {"center": v(-685.46, -800) * mm, "radius": 100 * mm});
            skCircle(sketch, "E61", {"center": v(-685.46, -800) * mm, "radius": 10 * mm});
            skSolve(sketch);
        }
        {
            var Q0;
            Q0 = qSketchRegion(id + "F54", true);
            extrude(context, id + "F55", {"entities" : qUnion([Q0]), "oppositeDirection" : true, "depth" : 50 * mm});
        }
        {
            var Q0;
            Q0=makeQuery(id+"F55.opExtrude","CAP_FACE",FACE,{"disambiguationData":[OSD([sQuery(id+"F54.wireOp",EDGE,"E60"),sQuery(id+"F54.wireOp",EDGE,"E61")])],"isStart":true});
            var sketch = newSketch(context, id + "F56", { "sketchPlane" : qUnion([Q0])});
            skCircle(sketch, "E62.0", {"center": v(-685.46, -800) * mm, "radius": 10 * mm});
            skSolve(sketch);
        }
        {
            var Q0;
            Q0 = qSketchRegion(id + "F56", true);
            extrude(context, id + "F57", {"entities" : qUnion([Q0]), "depth" : 25 * mm, "hasSecondDirection" : true, "secondDirectionOppositeDirection" : true, "secondDirectionDepth" : 60 * mm});
        }
        {
            var Q0;
            Q0=makeQuery(id+"F55.opExtrude","CAP_FACE",FACE,{"disambiguationData":[OSD([sQuery(id+"F54.wireOp",EDGE,"E60"),sQuery(id+"F54.wireOp",EDGE,"E61")])],"isStart":true});
            var sketch = newSketch(context, id + "F58", { "sketchPlane" : qUnion([Q0])});
            skLineSegment(sketch, "E63.bottom", {"start": v(-705.46, -787.5) * mm, "end": v(-452.14, -787.5) * mm});
            skLineSegment(sketch, "E63.top", {"start": v(-705.46, -812.5) * mm, "end": v(-452.14, -812.5) * mm});
            skLineSegment(sketch, "E63.left", {"start": v(-705.46, -787.5) * mm, "end": v(-705.46, -812.5) * mm});
            skLineSegment(sketch, "E63.right", {"start": v(-452.14, -787.5) * mm, "end": v(-452.14, -812.5) * mm});
            skCircle(sketch, "E64.0", {"center": v(-685.46, -800) * mm, "radius": 10 * mm, "construction": true});
            skLineSegment(sketch, "E65.0", {"start": v(-475, -900) * mm, "end": v(-452.14, -800) * mm, "construction": true});
            skLineSegment(sketch, "E66", {"start": v(-729.93, -800) * mm, "end": v(-388.96, -800) * mm, "construction": true});
            skLineSegment(sketch, "E67", {"start": v(-452.14, -800) * mm, "end": v(-275, -25) * mm, "construction": true});
            skSolve(sketch);
        }
        {
            var Q0;
            Q0 = qSketchRegion(id + "F58", true);
            extrude(context, id + "F59", {"entities" : qUnion([Q0]), "depth" : 25 * mm});
        }
        {
            var Q0;
            Q0=makeQuery(id+"F55.opExtrude","SWEPT_BODY",BODY,{"disambiguationData":[OSD([sQuery(id+"F54.wireOp",EDGE,"E60"),sQuery(id+"F54.wireOp",EDGE,"E61")])]});
            var Q1;
            Q1=makeQuery(id+"F59.opExtrude","SWEPT_BODY",BODY,{"disambiguationData":[OSD([sQuery(id+"F58.wireOp",EDGE,"E63.bottom"),sQuery(id+"F58.wireOp",EDGE,"E63.top"),sQuery(id+"F58.wireOp",EDGE,"E63.left"),sQuery(id+"F58.wireOp",EDGE,"E63.right")])]});
            var Q2;
            Q2=makeQuery(id+"F57.opExtrude","SWEPT_BODY",BODY,{"disambiguationData":[OSD([sQuery(id+"F56.wireOp",EDGE,"E62.0")])]});
            var Q3;
            Q3=qCreatedBy(makeId("Front.planeOp"),FACE);
            mirror(context, id + "F60", {"entities" : qUnion([Q0, Q1, Q2]), "mirrorPlane" : qUnion([Q3])});
        }
        {
            var Q0;
            Q0=makeQuery(id+"F17.opExtrude","CAP_FACE",FACE,{"disambiguationData":[OSD([sQuery(id+"F16.wireOp",EDGE,"E20.bottom"),sQuery(id+"F16.wireOp",EDGE,"E20.top"),sQuery(id+"F16.wireOp",EDGE,"E20.left"),sQuery(id+"F16.wireOp",EDGE,"E20.right")])],"isStart":false});
            shell(context, id + "F61", {"entities" : qUnion([Q0]), "thickness" : 3 * mm});
        }
        {
            var Q0;
            Q0=makeQuery(id+"F61.opShell","OFFSET_FACE",FACE,{"disambiguationData":[OSD([sQuery(id+"F16.wireOp",EDGE,"E20.bottom"),sQuery(id+"F16.wireOp",EDGE,"E20.top"),sQuery(id+"F16.wireOp",EDGE,"E20.left"),sQuery(id+"F16.wireOp",EDGE,"E20.right")])]});
            var sketch = newSketch(context, id + "F62", { "sketchPlane" : qUnion([Q0])});
            skLineSegment(sketch, "E68.bottom", {"start": v(-379.17, 267.8) * mm, "end": v(379.17, 267.8) * mm});
            skLineSegment(sketch, "E68.top", {"start": v(-379.17, -267.8) * mm, "end": v(379.17, -267.8) * mm});
            skLineSegment(sketch, "E68.left", {"start": v(-379.17, 267.8) * mm, "end": v(-379.17, -267.8) * mm});
            skLineSegment(sketch, "E68.right", {"start": v(379.17, 267.8) * mm, "end": v(379.17, -267.8) * mm});
            skSolve(sketch);
        }
        {
            var Q0;
            Q0 = qSketchRegion(id + "F62", true);
            extrude(context, id + "F63", {"entities" : qUnion([Q0]), "operationType" : NewBodyOperationType.REMOVE, "endBound" : BoundingType.THROUGH_ALL, "oppositeDirection" : true, "depth" : 25 * mm});
        }
        {
            var Q0;
            Q0=makeQuery(id+"F59.opExtrude","SWEPT_FACE",FACE,{"disambiguationData":[OSD([sQuery(id+"F58.wireOp",EDGE,"E63.left")])]});
            shell(context, id + "F64", {"entities" : qUnion([Q0]), "thickness" : 2 * mm});
        }
        {
            var Q0;
            Q0=makeQuery(id+"F60.opPattern","COPY",FACE,{"derivedFrom":makeQuery(id+"F59.opExtrude","SWEPT_FACE",FACE,{"disambiguationData":[OSD([sQuery(id+"F58.wireOp",EDGE,"E63.left")])]}),"instanceName":"1"});
            shell(context, id + "F65", {"entities" : qUnion([Q0]), "thickness" : 2 * mm});
        }
    });
